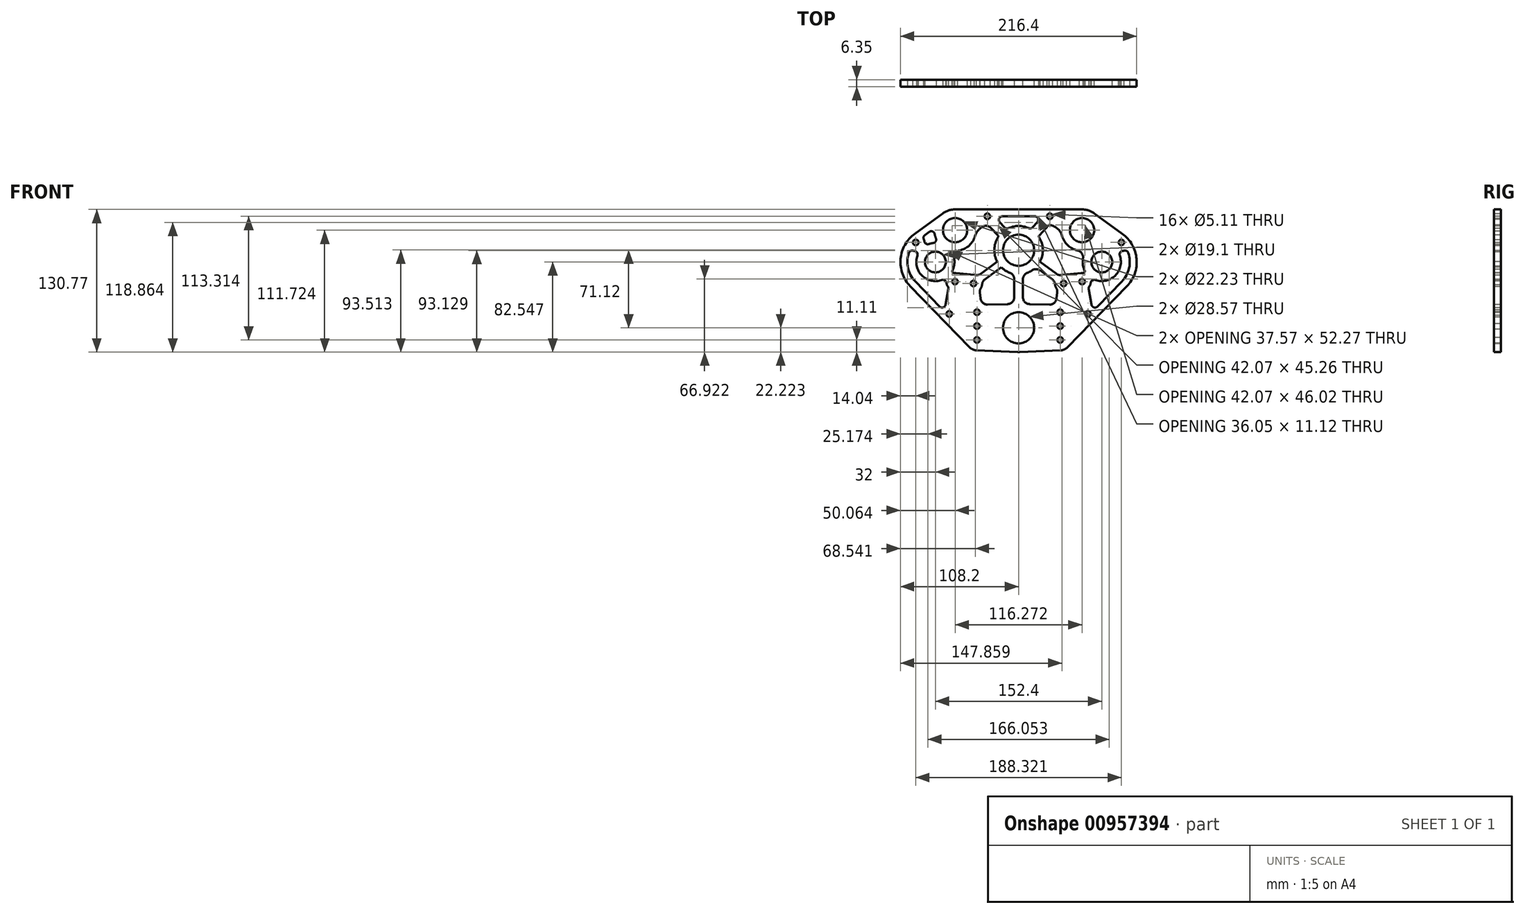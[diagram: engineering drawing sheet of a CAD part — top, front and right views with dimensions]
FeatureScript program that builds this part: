
annotation { "Feature Type Name" : "Feature", "Feature Type Description" : "" }
export const myFeature = defineFeature(function(context is Context, id is Id, definition is map)
    precondition{}
    {
        {
            var Q0;
            Q0=qCreatedBy(makeId("Front.planeOp"),FACE);
            var sketch = newSketch(context, id + "F0", { "sketchPlane" : qUnion([Q0])});
            skCircle(sketch, "E0", {"center": v(-76.2, 58.74) * mm, "radius": 32 * mm, "construction": true});
            skCircle(sketch, "E1", {"center": v(76.2, 58.74) * mm, "radius": 32 * mm, "construction": true});
            skLineSegment(sketch, "E2", {"start": v(-76.2, 58.74) * mm, "end": v(76.2, 58.74) * mm, "construction": true});
            skLineSegment(sketch, "E3", {"start": v(0, 58.74) * mm, "end": v(0, 0) * mm, "construction": true});
            skCircle(sketch, "E4", {"center": v(-76.2, 58.74) * mm, "radius": 7.63 * mm, "construction": true});
            skCircle(sketch, "E5", {"center": v(76.2, 58.74) * mm, "radius": 7.63 * mm, "construction": true});
            skLineSegment(sketch, "E6.bottom", {"start": v(-127, 23.81) * mm, "end": v(127, 23.81) * mm, "construction": true});
            skLineSegment(sketch, "E6.top", {"start": v(-127, -26.99) * mm, "end": v(127, -26.99) * mm, "construction": true});
            skLineSegment(sketch, "E6.left", {"start": v(-127, 23.81) * mm, "end": v(-127, -26.99) * mm, "construction": true});
            skLineSegment(sketch, "E6.right", {"start": v(127, 23.81) * mm, "end": v(127, -26.99) * mm, "construction": true});
            skPoint(sketch, "E6.middle", {"position": v(0, -1.59) * mm});
            skCircle(sketch, "E7", {"center": v(0, 0) * mm, "radius": 50.8 * mm, "construction": true});
            skCircle(sketch, "E8", {"center": v(-58.14, 87.91) * mm, "radius": 26.68 * mm, "construction": true});
            skCircle(sketch, "E9", {"center": v(58.14, 87.91) * mm, "radius": 26.68 * mm, "construction": true});
            skCircle(sketch, "E10", {"center": v(0, 69.53) * mm, "radius": 34.3 * mm, "construction": true});
            skCircle(sketch, "E11", {"center": v(0, 69.53) * mm, "radius": 25.4 * mm, "construction": true});
            skCircle(sketch, "E12", {"center": v(0, 69.53) * mm, "radius": 38.1 * mm, "construction": true});
            skCircle(sketch, "E13", {"center": v(0, -1.59) * mm, "radius": 33.02 * mm, "construction": true});
            skCircle(sketch, "E14", {"center": v(0, -1.59) * mm, "radius": 45.72 * mm, "construction": true});
            skCircle(sketch, "E15", {"center": v(-76.2, 58.74) * mm, "radius": 9.55 * mm});
            skCircle(sketch, "E16", {"center": v(76.2, 58.74) * mm, "radius": 9.55 * mm});
            skCircle(sketch, "E17", {"center": v(-58.14, 87.91) * mm, "radius": 11.11 * mm});
            skCircle(sketch, "E18", {"center": v(58.14, 87.91) * mm, "radius": 11.11 * mm});
            skCircle(sketch, "E19", {"center": v(0, 69.53) * mm, "radius": 14.29 * mm});
            skCircle(sketch, "E20", {"center": v(0, -1.59) * mm, "radius": 14.29 * mm});
            skCircle(sketch, "E21", {"center": v(-38.1, 12.7) * mm, "radius": 9.53 * mm, "construction": true});
            skCircle(sketch, "E22", {"center": v(-38.1, -12.7) * mm, "radius": 9.53 * mm, "construction": true});
            skCircle(sketch, "E23", {"center": v(38.1, -12.7) * mm, "radius": 9.53 * mm, "construction": true});
            skCircle(sketch, "E24", {"center": v(38.1, 12.7) * mm, "radius": 9.53 * mm, "construction": true});
            skCircle(sketch, "E25", {"center": v(38.1, 0) * mm, "radius": 9.53 * mm, "construction": true});
            skCircle(sketch, "E26", {"center": v(-38.1, 0) * mm, "radius": 9.53 * mm, "construction": true});
            skCircle(sketch, "E27", {"center": v(38.1, -12.7) * mm, "radius": 2.55 * mm});
            skCircle(sketch, "E28", {"center": v(38.1, 0) * mm, "radius": 2.55 * mm});
            skCircle(sketch, "E29", {"center": v(38.1, 12.7) * mm, "radius": 2.55 * mm});
            skCircle(sketch, "E30", {"center": v(-38.1, 12.7) * mm, "radius": 2.55 * mm});
            skCircle(sketch, "E31", {"center": v(-38.1, 0) * mm, "radius": 2.55 * mm});
            skCircle(sketch, "E32", {"center": v(-38.1, -12.7) * mm, "radius": 2.55 * mm});
            skLineSegment(sketch, "E33", {"start": v(-44.93, -19.34) * mm, "end": v(-99.15, 36.43) * mm});
            skArc(sketch, "E34", {"start": v(-44.93, -19.34) * mm, "mid": v(-42, -21.4) * mm, "end": v(-38.5, -22.22) * mm});
            skArc(sketch, "E35", {"start": v(38.5, -22.22) * mm, "mid": v(42, -21.4) * mm, "end": v(44.93, -19.34) * mm});
            skLineSegment(sketch, "E36", {"start": v(44.93, -19.34) * mm, "end": v(99.15, 36.43) * mm});
            skCircle(sketch, "E37", {"center": v(58.14, 87.91) * mm, "radius": 19.05 * mm, "construction": true});
            skCircle(sketch, "E38", {"center": v(-58.14, 87.91) * mm, "radius": 19.05 * mm, "construction": true});
            skArc(sketch, "E39", {"start": v(99.15, 36.43) * mm, "mid": v(108.09, 61.46) * mm, "end": v(95.04, 84.61) * mm});
            skArc(sketch, "E40", {"start": v(-95.04, 84.61) * mm, "mid": v(-108.09, 61.46) * mm, "end": v(-99.15, 36.43) * mm});
            skLineSegment(sketch, "E41", {"start": v(-58.24, 40.78) * mm, "end": v(-76.2, 58.74) * mm, "construction": true});
            skLineSegment(sketch, "E42", {"start": v(-76.2, 58.74) * mm, "end": v(-94.16, 76.7) * mm, "construction": true});
            skCircle(sketch, "E43", {"center": v(-94.16, 76.7) * mm, "radius": 2.55 * mm});
            skCircle(sketch, "E44", {"center": v(-58.24, 40.78) * mm, "radius": 2.55 * mm});
            skCircle(sketch, "E45.MirrorC", {"center": v(58.24, 40.78) * mm, "radius": 2.55 * mm});
            skLineSegment(sketch, "E46.MirrorCS", {"start": v(58.24, 40.78) * mm, "end": v(76.2, 58.74) * mm, "construction": true});
            skLineSegment(sketch, "E47.MirrorCS", {"start": v(76.2, 58.74) * mm, "end": v(94.16, 76.7) * mm, "construction": true});
            skCircle(sketch, "E48.MirrorC", {"center": v(94.16, 76.7) * mm, "radius": 2.55 * mm});
            skLineSegment(sketch, "E49", {"start": v(95.04, 84.61) * mm, "end": v(69.35, 103.31) * mm});
            skLineSegment(sketch, "E50", {"start": v(-95.04, 84.61) * mm, "end": v(-69.35, 103.31) * mm});
            skLineSegment(sketch, "E51", {"start": v(-58.14, 106.96) * mm, "end": v(58.14, 106.96) * mm});
            skArc(sketch, "E52", {"start": v(-69.35, 103.31) * mm, "mid": v(-64.03, 106.03) * mm, "end": v(-58.14, 106.96) * mm});
            skArc(sketch, "E53", {"start": v(58.14, 106.96) * mm, "mid": v(64.03, 106.03) * mm, "end": v(69.35, 103.31) * mm});
            skCircle(sketch, "E54", {"center": v(0, -1.59) * mm, "radius": 22.23 * mm, "construction": true});
            skLineSegment(sketch, "E55", {"start": v(38.5, -22.22) * mm, "end": v(0.93, -23.8) * mm});
            skLineSegment(sketch, "E56", {"start": v(-38.5, -22.22) * mm, "end": v(-0.93, -23.8) * mm});
            skArc(sketch, "E57", {"start": v(-0.93, -23.8) * mm, "mid": v(0, -23.81) * mm, "end": v(0.93, -23.8) * mm});
            skLineSegment(sketch, "E58.bottom", {"start": v(-38.1, -12.7) * mm, "end": v(38.1, -12.7) * mm, "construction": true});
            skLineSegment(sketch, "E58.top", {"start": v(-38.1, 12.7) * mm, "end": v(38.1, 12.7) * mm, "construction": true});
            skLineSegment(sketch, "E58.left", {"start": v(-38.1, -12.7) * mm, "end": v(-38.1, 12.7) * mm, "construction": true});
            skLineSegment(sketch, "E58.right", {"start": v(38.1, -12.7) * mm, "end": v(38.1, 12.7) * mm, "construction": true});
            skCircle(sketch, "E59", {"center": v(-28.58, 100.61) * mm, "radius": 6.35 * mm, "construction": true});
            skCircle(sketch, "E60", {"center": v(-28.58, 100.61) * mm, "radius": 2.55 * mm});
            skCircle(sketch, "E61.MirrorC", {"center": v(28.57, 100.61) * mm, "radius": 6.35 * mm, "construction": true});
            skCircle(sketch, "E62.MirrorC", {"center": v(28.57, 100.61) * mm, "radius": 2.55 * mm});
            skCircle(sketch, "E63", {"center": v(-63.5, 11.15) * mm, "radius": 7.94 * mm, "construction": true});
            skCircle(sketch, "E64", {"center": v(-63.5, 11.15) * mm, "radius": 2.55 * mm});
            skCircle(sketch, "E65.MirrorC", {"center": v(63.5, 11.15) * mm, "radius": 7.94 * mm, "construction": true});
            skCircle(sketch, "E66.MirrorC", {"center": v(63.5, 11.15) * mm, "radius": 2.55 * mm});
            skCircle(sketch, "E67", {"center": v(-41.28, 39.05) * mm, "radius": 6.35 * mm, "construction": true});
            skCircle(sketch, "E68", {"center": v(41.28, 39.05) * mm, "radius": 6.35 * mm, "construction": true});
            skCircle(sketch, "E69", {"center": v(41.28, 39.05) * mm, "radius": 2.55 * mm});
            skCircle(sketch, "E70", {"center": v(-41.28, 39.05) * mm, "radius": 2.55 * mm});
            skLineSegment(sketch, "E71", {"start": v(41.28, 39.05) * mm, "end": v(-41.28, 39.05) * mm, "construction": true});
            skLineSegment(sketch, "E72", {"start": v(0, 39.05) * mm, "end": v(0, 69.53) * mm, "construction": true});
            skSolve(sketch);
        }
        {
            var Q0;
            Q0 = qSketchRegion(id + "F0", true);
            extrude(context, id + "F1", {"entities" : qUnion([Q0]), "depth" : 6.35 * mm, "offsetDistance" : 25.4 * mm});
        }
        {
            var Q0;
            Q0=makeQuery(id+"F1.opExtrude","CAP_FACE",FACE,{"disambiguationData":[OSD([sQuery(id+"F0.wireOp",EDGE,"E15"),sQuery(id+"F0.wireOp",EDGE,"E16"),sQuery(id+"F0.wireOp",EDGE,"E17"),sQuery(id+"F0.wireOp",EDGE,"E18"),sQuery(id+"F0.wireOp",EDGE,"E19"),sQuery(id+"F0.wireOp",EDGE,"E20"),sQuery(id+"F0.wireOp",EDGE,"E27"),sQuery(id+"F0.wireOp",EDGE,"E28"),sQuery(id+"F0.wireOp",EDGE,"E29"),sQuery(id+"F0.wireOp",EDGE,"E30"),sQuery(id+"F0.wireOp",EDGE,"E31"),sQuery(id+"F0.wireOp",EDGE,"E32"),sQuery(id+"F0.wireOp",EDGE,"E33"),sQuery(id+"F0.wireOp",EDGE,"E34"),sQuery(id+"F0.wireOp",EDGE,"E35"),sQuery(id+"F0.wireOp",EDGE,"E36"),sQuery(id+"F0.wireOp",EDGE,"E39"),sQuery(id+"F0.wireOp",EDGE,"E40"),sQuery(id+"F0.wireOp",EDGE,"E43"),sQuery(id+"F0.wireOp",EDGE,"E44"),sQuery(id+"F0.wireOp",EDGE,"E45.MirrorC"),sQuery(id+"F0.wireOp",EDGE,"E48.MirrorC"),sQuery(id+"F0.wireOp",EDGE,"E49"),sQuery(id+"F0.wireOp",EDGE,"E50"),sQuery(id+"F0.wireOp",EDGE,"E51"),sQuery(id+"F0.wireOp",EDGE,"E52"),sQuery(id+"F0.wireOp",EDGE,"E53"),sQuery(id+"F0.wireOp",EDGE,"E55"),sQuery(id+"F0.wireOp",EDGE,"E56"),sQuery(id+"F0.wireOp",EDGE,"E57"),sQuery(id+"F0.wireOp",EDGE,"E60"),sQuery(id+"F0.wireOp",EDGE,"E62.MirrorC"),sQuery(id+"F0.wireOp",EDGE,"E64"),sQuery(id+"F0.wireOp",EDGE,"E66.MirrorC"),sQuery(id+"F0.wireOp",EDGE,"E69"),sQuery(id+"F0.wireOp",EDGE,"E70")])],"isStart":false});
            var sketch = newSketch(context, id + "F2", { "sketchPlane" : qUnion([Q0])});
            skCircle(sketch, "E73", {"center": v(-58.14, 87.91) * mm, "radius": 19.05 * mm, "construction": true});
            skCircle(sketch, "E74", {"center": v(0, 69.53) * mm, "radius": 22.23 * mm, "construction": true});
            skCircle(sketch, "E75", {"center": v(58.14, 87.91) * mm, "radius": 19.05 * mm, "construction": true});
            skCircle(sketch, "E76", {"center": v(76.2, 58.74) * mm, "radius": 17.49 * mm, "construction": true});
            skCircle(sketch, "E77", {"center": v(94.16, 76.7) * mm, "radius": 7.94 * mm, "construction": true});
            skCircle(sketch, "E78", {"center": v(58.24, 40.78) * mm, "radius": 7.94 * mm, "construction": true});
            skCircle(sketch, "E79", {"center": v(41.28, 39.05) * mm, "radius": 7.94 * mm, "construction": true});
            skCircle(sketch, "E80", {"center": v(63.5, 11.15) * mm, "radius": 7.94 * mm, "construction": true});
            skCircle(sketch, "E81", {"center": v(38.1, 12.7) * mm, "radius": 7.94 * mm, "construction": true});
            skCircle(sketch, "E82", {"center": v(38.1, 0) * mm, "radius": 7.94 * mm, "construction": true});
            skCircle(sketch, "E83", {"center": v(38.1, -12.7) * mm, "radius": 7.94 * mm, "construction": true});
            skCircle(sketch, "E84", {"center": v(-38.1, 12.7) * mm, "radius": 7.94 * mm, "construction": true});
            skCircle(sketch, "E85", {"center": v(-38.1, 0) * mm, "radius": 7.94 * mm, "construction": true});
            skCircle(sketch, "E86", {"center": v(-38.1, -12.7) * mm, "radius": 7.94 * mm, "construction": true});
            skCircle(sketch, "E87", {"center": v(-63.5, 11.15) * mm, "radius": 7.94 * mm, "construction": true});
            skCircle(sketch, "E88", {"center": v(-41.28, 39.05) * mm, "radius": 7.94 * mm, "construction": true});
            skCircle(sketch, "E89", {"center": v(-58.24, 40.78) * mm, "radius": 7.94 * mm, "construction": true});
            skCircle(sketch, "E90", {"center": v(-76.2, 58.74) * mm, "radius": 17.49 * mm, "construction": true});
            skCircle(sketch, "E91", {"center": v(-94.16, 76.7) * mm, "radius": 7.94 * mm, "construction": true});
            skCircle(sketch, "E92", {"center": v(-28.58, 100.61) * mm, "radius": 7.94 * mm, "construction": true});
            skCircle(sketch, "E93", {"center": v(28.57, 100.61) * mm, "radius": 7.94 * mm, "construction": true});
            skCircle(sketch, "E94", {"center": v(0, -1.59) * mm, "radius": 22.23 * mm, "construction": true});
            skLineSegment(sketch, "E95", {"start": v(-99.15, 36.43) * mm, "end": v(-44.93, -19.34) * mm, "construction": true});
            skLineSegment(sketch, "E96", {"start": v(-38.5, -22.22) * mm, "end": v(-0.93, -23.8) * mm, "construction": true});
            skLineSegment(sketch, "E97", {"start": v(0.93, -23.8) * mm, "end": v(38.5, -22.22) * mm, "construction": true});
            skLineSegment(sketch, "E98", {"start": v(44.93, -19.34) * mm, "end": v(99.15, 36.43) * mm, "construction": true});
            skLineSegment(sketch, "E99", {"start": v(95.04, 84.61) * mm, "end": v(69.35, 103.31) * mm, "construction": true});
            skLineSegment(sketch, "E100", {"start": v(58.14, 106.96) * mm, "end": v(-58.14, 106.96) * mm, "construction": true});
            skLineSegment(sketch, "E101", {"start": v(-69.35, 103.31) * mm, "end": v(-95.04, 84.61) * mm, "construction": true});
            skArc(sketch, "E102", {"start": v(-58.14, 106.96) * mm, "mid": v(-64.03, 106.03) * mm, "end": v(-69.35, 103.31) * mm, "construction": true});
            skArc(sketch, "E103", {"start": v(-95.04, 84.61) * mm, "mid": v(-108.09, 61.46) * mm, "end": v(-99.15, 36.43) * mm, "construction": true});
            skArc(sketch, "E104", {"start": v(-44.93, -19.34) * mm, "mid": v(-42, -21.4) * mm, "end": v(-38.5, -22.22) * mm, "construction": true});
            skArc(sketch, "E105", {"start": v(-0.93, -23.8) * mm, "mid": v(0, -23.81) * mm, "end": v(0.93, -23.8) * mm, "construction": true});
            skArc(sketch, "E106", {"start": v(38.5, -22.22) * mm, "mid": v(42, -21.4) * mm, "end": v(44.93, -19.34) * mm, "construction": true});
            skArc(sketch, "E107", {"start": v(99.15, 36.43) * mm, "mid": v(108.09, 61.46) * mm, "end": v(95.04, 84.61) * mm, "construction": true});
            skLineSegment(sketch, "E108.0", {"start": v(58.14, 100.61) * mm, "end": v(-58.14, 100.61) * mm, "construction": true});
            skArc(sketch, "E108.1", {"start": v(58.14, 100.61) * mm, "mid": v(62.07, 99.99) * mm, "end": v(65.61, 98.18) * mm, "construction": true});
            skLineSegment(sketch, "E108.2", {"start": v(91.3, 79.48) * mm, "end": v(65.61, 98.18) * mm, "construction": true});
            skArc(sketch, "E108.3", {"start": v(-40.38, -14.91) * mm, "mid": v(-39.4, -15.6) * mm, "end": v(-38.23, -15.87) * mm, "construction": true});
            skLineSegment(sketch, "E108.4", {"start": v(-94.6, 40.85) * mm, "end": v(-40.38, -14.91) * mm, "construction": true});
            skArc(sketch, "E108.5", {"start": v(-91.3, 79.48) * mm, "mid": v(-101.76, 60.92) * mm, "end": v(-94.6, 40.85) * mm, "construction": true});
            skLineSegment(sketch, "E108.6", {"start": v(-65.61, 98.18) * mm, "end": v(-91.3, 79.48) * mm, "construction": true});
            skLineSegment(sketch, "E108.7", {"start": v(-38.23, -15.87) * mm, "end": v(-0.67, -17.45) * mm, "construction": true});
            skArc(sketch, "E108.8", {"start": v(-0.67, -17.45) * mm, "mid": v(0, -17.46) * mm, "end": v(0.67, -17.45) * mm, "construction": true});
            skLineSegment(sketch, "E108.9", {"start": v(0.67, -17.45) * mm, "end": v(38.23, -15.87) * mm, "construction": true});
            skArc(sketch, "E108.10", {"start": v(-58.14, 100.61) * mm, "mid": v(-62.07, 99.99) * mm, "end": v(-65.61, 98.18) * mm, "construction": true});
            skArc(sketch, "E108.11", {"start": v(38.23, -15.87) * mm, "mid": v(39.4, -15.6) * mm, "end": v(40.38, -14.91) * mm, "construction": true});
            skLineSegment(sketch, "E108.12", {"start": v(40.38, -14.91) * mm, "end": v(94.6, 40.85) * mm, "construction": true});
            skArc(sketch, "E108.13", {"start": v(94.6, 40.85) * mm, "mid": v(101.76, 60.92) * mm, "end": v(91.3, 79.48) * mm, "construction": true});
            skArc(sketch, "E109", {"start": v(-59, 61.93) * mm, "mid": v(-58.88, 56.32) * mm, "end": v(-60.53, 50.97) * mm});
            skArc(sketch, "E110", {"start": v(-58.97, 48.68) * mm, "mid": v(-58.2, 48.71) * mm, "end": v(-57.44, 48.67) * mm});
            skLineSegment(sketch, "E111", {"start": v(-57.44, 48.67) * mm, "end": v(-40.47, 46.95) * mm});
            skLineSegment(sketch, "E112", {"start": v(-41.28, 39.05) * mm, "end": v(0, 69.53) * mm, "construction": true});
            skLineSegment(sketch, "E113", {"start": v(-34.6, 47.93) * mm, "end": v(-19.58, 59.02) * mm});
            skLineSegment(sketch, "E114", {"start": v(-33.54, 40.82) * mm, "end": v(-15.8, 53.91) * mm});
            skLineSegment(sketch, "E115", {"start": v(-28.45, 52.47) * mm, "end": v(-26.56, 49.92) * mm, "construction": true});
            skLineSegment(sketch, "E116", {"start": v(-24.67, 47.37) * mm, "end": v(-26.56, 49.92) * mm, "construction": true});
            skArc(sketch, "E117", {"start": v(-40.47, 46.95) * mm, "mid": v(-40.06, 46.9) * mm, "end": v(-39.66, 46.82) * mm});
            skArc(sketch, "E118", {"start": v(-19.58, 59.02) * mm, "mid": v(-22.21, 70.25) * mm, "end": v(-18.86, 81.3) * mm});
            skLineSegment(sketch, "E119", {"start": v(0, 69.53) * mm, "end": v(-28.58, 100.61) * mm, "construction": true});
            skLineSegment(sketch, "E120", {"start": v(-19.04, 83.2) * mm, "end": v(-25.2, 89.9) * mm});
            skArc(sketch, "E121", {"start": v(-32.76, 91.25) * mm, "mid": v(-37.18, 87.69) * mm, "end": v(-39.82, 82.66) * mm});
            skArc(sketch, "E122", {"start": v(-54.1, 69.3) * mm, "mid": v(-45.12, 74) * mm, "end": v(-39.82, 82.66) * mm});
            skPoint(sketch, "E123.visualSharp", {"position": v(-62.28, 69.32) * mm});
            skArc(sketch, "E123.filletArc", {"start": v(-54.1, 69.3) * mm, "mid": v(-58.05, 66.6) * mm, "end": v(-59, 61.93) * mm});
            skPoint(sketch, "E124.visualSharp", {"position": v(-37.3, 45.93) * mm});
            skArc(sketch, "E124.filletArc", {"start": v(-39.66, 46.82) * mm, "mid": v(-37, 46.84) * mm, "end": v(-34.6, 47.93) * mm});
            skPoint(sketch, "E125.visualSharp", {"position": v(-63.47, 46.75) * mm});
            skArc(sketch, "E125.filletArc", {"start": v(-60.53, 50.97) * mm, "mid": v(-60.42, 49.36) * mm, "end": v(-58.97, 48.68) * mm});
            skPoint(sketch, "E126.visualSharp", {"position": v(-18.2, 82.3) * mm});
            skArc(sketch, "E126.filletArc", {"start": v(-18.86, 81.3) * mm, "mid": v(-18.63, 82.28) * mm, "end": v(-19.04, 83.2) * mm});
            skLineSegment(sketch, "E127", {"start": v(0, 69.53) * mm, "end": v(0, 0) * mm, "construction": true});
            skArc(sketch, "E128.MirrorCS", {"start": v(58.97, 48.68) * mm, "mid": v(58.2, 48.71) * mm, "end": v(57.44, 48.67) * mm});
            skArc(sketch, "E129.MirrorCS", {"start": v(60.53, 50.97) * mm, "mid": v(60.42, 49.36) * mm, "end": v(58.97, 48.68) * mm});
            skArc(sketch, "E130.MirrorCS", {"start": v(18.86, 81.3) * mm, "mid": v(18.63, 82.28) * mm, "end": v(19.04, 83.2) * mm});
            skLineSegment(sketch, "E131.MirrorCS", {"start": v(28.45, 52.47) * mm, "end": v(26.56, 49.92) * mm, "construction": true});
            skArc(sketch, "E132.MirrorCS", {"start": v(40.47, 46.95) * mm, "mid": v(40.06, 46.9) * mm, "end": v(39.66, 46.82) * mm});
            skArc(sketch, "E133.MirrorCS", {"start": v(39.66, 46.82) * mm, "mid": v(37, 46.84) * mm, "end": v(34.6, 47.93) * mm});
            skLineSegment(sketch, "E134.MirrorCS", {"start": v(24.67, 47.37) * mm, "end": v(26.56, 49.92) * mm, "construction": true});
            skArc(sketch, "E135.MirrorCS", {"start": v(54.1, 69.3) * mm, "mid": v(45.12, 74) * mm, "end": v(39.82, 82.66) * mm});
            skArc(sketch, "E136.MirrorCS", {"start": v(19.58, 59.02) * mm, "mid": v(22.21, 70.25) * mm, "end": v(18.86, 81.3) * mm});
            skPoint(sketch, "E137.MirrorP", {"position": v(37.3, 45.93) * mm});
            skLineSegment(sketch, "E138.MirrorCS", {"start": v(57.44, 48.67) * mm, "end": v(40.47, 46.95) * mm});
            skArc(sketch, "E139.MirrorCS", {"start": v(27.78, 92.72) * mm, "mid": v(35.35, 89.54) * mm, "end": v(39.82, 82.66) * mm});
            skLineSegment(sketch, "E140.MirrorCS", {"start": v(33.54, 40.82) * mm, "end": v(15.8, 53.91) * mm});
            skPoint(sketch, "E141.MirrorP", {"position": v(63.47, 46.75) * mm});
            skLineSegment(sketch, "E142.MirrorCS", {"start": v(34.6, 47.93) * mm, "end": v(19.58, 59.02) * mm});
            skArc(sketch, "E143.MirrorCS", {"start": v(54.1, 69.3) * mm, "mid": v(58.05, 66.6) * mm, "end": v(59, 61.93) * mm});
            skLineSegment(sketch, "E144.MirrorCS", {"start": v(19.04, 83.2) * mm, "end": v(27.78, 92.72) * mm});
            skPoint(sketch, "E145.MirrorP", {"position": v(18.2, 82.3) * mm});
            skArc(sketch, "E146.MirrorCS", {"start": v(59, 61.93) * mm, "mid": v(58.88, 56.32) * mm, "end": v(60.53, 50.97) * mm});
            skLineSegment(sketch, "E147.MirrorCS", {"start": v(-58.14, 100.61) * mm, "end": v(58.14, 100.61) * mm, "construction": true});
            skPoint(sketch, "E148.MirrorP", {"position": v(62.28, 69.32) * mm});
            skLineSegment(sketch, "E149", {"start": v(-11.19, 88.74) * mm, "end": v(-20.77, 99.16) * mm, "construction": true});
            skLineSegment(sketch, "E150", {"start": v(11.19, 88.74) * mm, "end": v(20.77, 99.16) * mm, "construction": true});
            skArc(sketch, "E151", {"start": v(-9.18, 89.77) * mm, "mid": v(0, 91.76) * mm, "end": v(9.18, 89.77) * mm});
            skLineSegment(sketch, "E152", {"start": v(0, 69.53) * mm, "end": v(28.57, 100.61) * mm, "construction": true});
            skLineSegment(sketch, "E153", {"start": v(0, 69.53) * mm, "end": v(41.28, 39.05) * mm, "construction": true});
            skLineSegment(sketch, "E154", {"start": v(-14.87, 100.61) * mm, "end": v(14.87, 100.61) * mm});
            skLineSegment(sketch, "E155", {"start": v(12.82, 90.52) * mm, "end": v(17.21, 95.29) * mm});
            skLineSegment(sketch, "E156", {"start": v(-12.82, 90.52) * mm, "end": v(-17.21, 95.29) * mm});
            skPoint(sketch, "E157.visualSharp", {"position": v(-22.1, 100.61) * mm});
            skArc(sketch, "E157.filletArc", {"start": v(-14.87, 100.61) * mm, "mid": v(-17.78, 98.71) * mm, "end": v(-17.21, 95.29) * mm});
            skPoint(sketch, "E158.visualSharp", {"position": v(-11.19, 88.74) * mm});
            skArc(sketch, "E158.filletArc", {"start": v(-12.82, 90.52) * mm, "mid": v(-11.12, 89.56) * mm, "end": v(-9.18, 89.77) * mm});
            skPoint(sketch, "E159.visualSharp", {"position": v(11.19, 88.74) * mm});
            skArc(sketch, "E159.filletArc", {"start": v(9.18, 89.77) * mm, "mid": v(11.12, 89.56) * mm, "end": v(12.82, 90.52) * mm});
            skPoint(sketch, "E160.visualSharp", {"position": v(22.1, 100.61) * mm});
            skArc(sketch, "E160.filletArc", {"start": v(17.21, 95.29) * mm, "mid": v(17.78, 98.71) * mm, "end": v(14.87, 100.61) * mm});
            skArc(sketch, "E161", {"start": v(-96.5, 69.12) * mm, "mid": v(-95.87, 68.95) * mm, "end": v(-95.23, 68.83) * mm});
            skArc(sketch, "E162", {"start": v(-92.67, 64.62) * mm, "mid": v(-88.57, 46.37) * mm, "end": v(-70.32, 42.27) * mm});
            skLineSegment(sketch, "E163", {"start": v(-58.24, 40.78) * mm, "end": v(-63.5, 11.15) * mm, "construction": true});
            skLineSegment(sketch, "E164", {"start": v(-64.29, 33.95) * mm, "end": v(-66.83, 19.64) * mm});
            skArc(sketch, "E165", {"start": v(-64.8, 36.3) * mm, "mid": v(-65.65, 37.93) * mm, "end": v(-66.1, 39.7) * mm});
            skArc(sketch, "E166", {"start": v(-68.16, 17.57) * mm, "mid": v(-68.14, 17.6) * mm, "end": v(-68.11, 17.6) * mm});
            skLineSegment(sketch, "E167", {"start": v(-72.3, 17.93) * mm, "end": v(-94.6, 40.85) * mm});
            skArc(sketch, "E168", {"start": v(-100.45, 67.12) * mm, "mid": v(-101.24, 53.16) * mm, "end": v(-94.6, 40.85) * mm});
            skPoint(sketch, "E169.visualSharp", {"position": v(-99.03, 70.43) * mm});
            skArc(sketch, "E169.filletArc", {"start": v(-96.5, 69.12) * mm, "mid": v(-98.88, 68.91) * mm, "end": v(-100.45, 67.12) * mm});
            skPoint(sketch, "E170.visualSharp", {"position": v(-88.93, 70.73) * mm});
            skArc(sketch, "E170.filletArc", {"start": v(-92.67, 64.62) * mm, "mid": v(-92.95, 67.34) * mm, "end": v(-95.23, 68.83) * mm});
            skPoint(sketch, "E171.visualSharp", {"position": v(-64.21, 46) * mm});
            skArc(sketch, "E171.filletArc", {"start": v(-66.1, 39.7) * mm, "mid": v(-67.6, 42) * mm, "end": v(-70.32, 42.27) * mm});
            skPoint(sketch, "E172.visualSharp", {"position": v(-64.04, 35.36) * mm});
            skArc(sketch, "E172.filletArc", {"start": v(-64.29, 33.95) * mm, "mid": v(-64.31, 35.17) * mm, "end": v(-64.8, 36.3) * mm});
            skPoint(sketch, "E173.visualSharp", {"position": v(-67.08, 18.23) * mm});
            skArc(sketch, "E173.filletArc", {"start": v(-68.11, 17.6) * mm, "mid": v(-67.27, 18.5) * mm, "end": v(-66.83, 19.64) * mm});
            skPoint(sketch, "E174.visualSharp", {"position": v(-70.06, 15.62) * mm});
            skArc(sketch, "E174.filletArc", {"start": v(-72.3, 17.93) * mm, "mid": v(-70.3, 16.98) * mm, "end": v(-68.16, 17.57) * mm});
            skArc(sketch, "E175.MirrorCS", {"start": v(68.16, 17.57) * mm, "mid": v(68.14, 17.6) * mm, "end": v(68.11, 17.6) * mm});
            skArc(sketch, "E176.MirrorCS", {"start": v(68.11, 17.6) * mm, "mid": v(67.27, 18.5) * mm, "end": v(66.83, 19.64) * mm});
            skArc(sketch, "E177.MirrorCS", {"start": v(96.5, 69.12) * mm, "mid": v(95.87, 68.95) * mm, "end": v(95.23, 68.83) * mm});
            skArc(sketch, "E178.MirrorCS", {"start": v(64.29, 33.95) * mm, "mid": v(64.31, 35.17) * mm, "end": v(64.8, 36.3) * mm});
            skArc(sketch, "E179.MirrorCS", {"start": v(64.8, 36.3) * mm, "mid": v(65.65, 37.93) * mm, "end": v(66.1, 39.7) * mm});
            skArc(sketch, "E180.MirrorCS", {"start": v(72.3, 17.93) * mm, "mid": v(70.3, 16.98) * mm, "end": v(68.16, 17.57) * mm});
            skArc(sketch, "E181.MirrorCS", {"start": v(92.67, 64.62) * mm, "mid": v(92.95, 67.34) * mm, "end": v(95.23, 68.83) * mm});
            skArc(sketch, "E182.MirrorCS", {"start": v(96.5, 69.12) * mm, "mid": v(98.88, 68.91) * mm, "end": v(100.45, 67.12) * mm});
            skPoint(sketch, "E183.MirrorP", {"position": v(64.21, 46) * mm});
            skLineSegment(sketch, "E184.MirrorCS", {"start": v(72.3, 17.93) * mm, "end": v(94.6, 40.85) * mm});
            skPoint(sketch, "E185.MirrorP", {"position": v(70.06, 15.62) * mm});
            skPoint(sketch, "E186.MirrorP", {"position": v(99.03, 70.43) * mm});
            skArc(sketch, "E187.MirrorCS", {"start": v(100.45, 67.12) * mm, "mid": v(101.24, 53.16) * mm, "end": v(94.6, 40.85) * mm});
            skLineSegment(sketch, "E188.MirrorCS", {"start": v(64.29, 33.95) * mm, "end": v(66.83, 19.64) * mm});
            skPoint(sketch, "E189.MirrorP", {"position": v(88.93, 70.73) * mm});
            skPoint(sketch, "E190.MirrorP", {"position": v(64.04, 35.36) * mm});
            skPoint(sketch, "E191.MirrorP", {"position": v(67.08, 18.23) * mm});
            skArc(sketch, "E192.MirrorCS", {"start": v(92.67, 64.62) * mm, "mid": v(88.57, 46.37) * mm, "end": v(70.32, 42.27) * mm});
            skArc(sketch, "E193.MirrorCS", {"start": v(66.1, 39.7) * mm, "mid": v(67.6, 42) * mm, "end": v(70.32, 42.27) * mm});
            skPoint(sketch, "E194.visualSharp", {"position": v(-27.78, 92.72) * mm});
            skArc(sketch, "E194.filletArc", {"start": v(-25.2, 89.9) * mm, "mid": v(-28.75, 91.85) * mm, "end": v(-32.76, 91.25) * mm});
            skLineSegment(sketch, "E195", {"start": v(-85.76, 83.51) * mm, "end": v(-81.84, 86.36) * mm});
            skArc(sketch, "E196", {"start": v(-76.86, 84.38) * mm, "mid": v(-76.37, 82.4) * mm, "end": v(-75.68, 80.5) * mm});
            skArc(sketch, "E197", {"start": v(-78.24, 76.1) * mm, "mid": v(-80.18, 75.77) * mm, "end": v(-82.08, 75.2) * mm});
            skArc(sketch, "E198", {"start": v(-86.83, 79.73) * mm, "mid": v(-86.5, 78.77) * mm, "end": v(-86.3, 77.77) * mm});
            skPoint(sketch, "E199.visualSharp", {"position": v(-88.1, 81.81) * mm});
            skArc(sketch, "E199.filletArc", {"start": v(-85.76, 83.51) * mm, "mid": v(-86.95, 81.8) * mm, "end": v(-86.83, 79.73) * mm});
            skPoint(sketch, "E200.visualSharp", {"position": v(-72.93, 75.92) * mm});
            skArc(sketch, "E200.filletArc", {"start": v(-78.24, 76.1) * mm, "mid": v(-75.86, 77.66) * mm, "end": v(-75.68, 80.5) * mm});
            skPoint(sketch, "E201.visualSharp", {"position": v(-88.19, 71.47) * mm});
            skArc(sketch, "E201.filletArc", {"start": v(-86.3, 77.77) * mm, "mid": v(-84.8, 75.48) * mm, "end": v(-82.08, 75.2) * mm});
            skPoint(sketch, "E202.visualSharp", {"position": v(-77.1, 89.82) * mm});
            skArc(sketch, "E202.filletArc", {"start": v(-76.86, 84.38) * mm, "mid": v(-78.8, 86.75) * mm, "end": v(-81.84, 86.36) * mm});
            skLineSegment(sketch, "E203", {"start": v(-38.1, 12.7) * mm, "end": v(-63.5, 11.15) * mm, "construction": true});
            skLineSegment(sketch, "E204", {"start": v(-38.58, 20.62) * mm, "end": v(-63.98, 19.07) * mm, "construction": true});
            skArc(sketch, "E205", {"start": v(-63.98, 19.07) * mm, "mid": v(-63.96, 3.22) * mm, "end": v(-62.11, 18.96) * mm, "construction": true});
            skLineSegment(sketch, "E206", {"start": v(63.5, 11.15) * mm, "end": v(58.24, 40.78) * mm, "construction": true});
            skLineSegment(sketch, "E207", {"start": v(38.1, 12.7) * mm, "end": v(63.5, 11.15) * mm, "construction": true});
            skLineSegment(sketch, "E208", {"start": v(58.24, 40.78) * mm, "end": v(41.28, 39.05) * mm, "construction": true});
            skCircle(sketch, "E209.MirrorC", {"center": v(-41.27, 39.05) * mm, "radius": 7.94 * mm, "construction": true});
            skLineSegment(sketch, "E210", {"start": v(-3.97, 47.66) * mm, "end": v(-3.97, 20.28) * mm});
            skLineSegment(sketch, "E211", {"start": v(3.97, 20.28) * mm, "end": v(3.97, 47.66) * mm});
            skLineSegment(sketch, "E212", {"start": v(-3.97, 33.97) * mm, "end": v(0, 33.97) * mm, "construction": true});
            skLineSegment(sketch, "E213", {"start": v(0, 33.97) * mm, "end": v(3.97, 33.97) * mm, "construction": true});
            skArc(sketch, "E214", {"start": v(-3.97, 47.66) * mm, "mid": v(-10.37, 49.88) * mm, "end": v(-15.8, 53.91) * mm});
            skArc(sketch, "E215", {"start": v(3.97, 47.66) * mm, "mid": v(10.37, 49.88) * mm, "end": v(15.8, 53.91) * mm});
            skLineSegment(sketch, "E216", {"start": v(-41.28, 39.05) * mm, "end": v(-38.1, 12.7) * mm, "construction": true});
            skLineSegment(sketch, "E217", {"start": v(-35.79, 33.32) * mm, "end": v(-34.13, 19.57) * mm});
            skLineSegment(sketch, "E218", {"start": v(-34.13, 19.57) * mm, "end": v(-3.97, 20.28) * mm});
            skArc(sketch, "E219", {"start": v(-35.79, 33.32) * mm, "mid": v(-33.67, 36.77) * mm, "end": v(-33.54, 40.82) * mm});
            skArc(sketch, "E220", {"start": v(33.54, 40.82) * mm, "mid": v(33.67, 36.77) * mm, "end": v(35.79, 33.32) * mm});
            skLineSegment(sketch, "E221", {"start": v(35.79, 33.32) * mm, "end": v(34.13, 19.57) * mm});
            skLineSegment(sketch, "E222", {"start": v(3.97, 20.28) * mm, "end": v(34.13, 19.57) * mm});
            skArc(sketch, "E223", {"start": v(-15.8, 53.91) * mm, "mid": v(-10.37, 49.88) * mm, "end": v(-3.97, 47.66) * mm});
            skSolve(sketch);
        }
        {
            var Q0;
            Q0 = qSketchRegion(id + "F2", true);
            extrude(context, id + "F3", {"entities" : qUnion([Q0]), "operationType" : NewBodyOperationType.REMOVE, "endBound" : BoundingType.THROUGH_ALL, "oppositeDirection" : true, "depth" : 25.4 * mm, "offsetDistance" : 25.4 * mm});
        }
        {
            var Q0;
            Q0=makeQuery(id+"F3.boolean.opBoolean","COPY",EDGE,{"derivedFrom":makeQuery(id+"F3.opExtrude","SWEPT_EDGE",EDGE,{"disambiguationData":[OSD([sQuery(id+"F2.wireOp",EDGE,"E114"),sQuery(id+"F2.wireOp",EDGE,"E223")])]})});
            var Q1;
            Q1=makeQuery(id+"F3.boolean.opBoolean","COPY",EDGE,{"derivedFrom":makeQuery(id+"F3.opExtrude","SWEPT_EDGE",EDGE,{"disambiguationData":[OSD([sQuery(id+"F2.wireOp",EDGE,"E114"),sQuery(id+"F2.wireOp",EDGE,"E219")])]})});
            var Q2;
            Q2=makeQuery(id+"F3.boolean.opBoolean","COPY",EDGE,{"derivedFrom":makeQuery(id+"F3.opExtrude","SWEPT_EDGE",EDGE,{"disambiguationData":[OSD([sQuery(id+"F2.wireOp",EDGE,"E217"),sQuery(id+"F2.wireOp",EDGE,"E219")])]})});
            var Q3;
            Q3=makeQuery(id+"F3.boolean.opBoolean","COPY",EDGE,{"derivedFrom":makeQuery(id+"F3.opExtrude","SWEPT_EDGE",EDGE,{"disambiguationData":[OSD([sQuery(id+"F2.wireOp",EDGE,"E210"),sQuery(id+"F2.wireOp",EDGE,"E223")])]})});
            var Q4;
            Q4=makeQuery(id+"F3.boolean.opBoolean","COPY",EDGE,{"derivedFrom":makeQuery(id+"F3.opExtrude","SWEPT_EDGE",EDGE,{"disambiguationData":[OSD([sQuery(id+"F2.wireOp",EDGE,"E210"),sQuery(id+"F2.wireOp",EDGE,"E218")])]})});
            var Q5;
            Q5=makeQuery(id+"F3.boolean.opBoolean","COPY",EDGE,{"derivedFrom":makeQuery(id+"F3.opExtrude","SWEPT_EDGE",EDGE,{"disambiguationData":[OSD([sQuery(id+"F2.wireOp",EDGE,"E217"),sQuery(id+"F2.wireOp",EDGE,"E218")])]})});
            var Q6;
            Q6=makeQuery(id+"F3.boolean.opBoolean","COPY",EDGE,{"derivedFrom":makeQuery(id+"F3.opExtrude","SWEPT_EDGE",EDGE,{"disambiguationData":[OSD([sQuery(id+"F2.wireOp",EDGE,"E211"),sQuery(id+"F2.wireOp",EDGE,"E222")])]})});
            var Q7;
            Q7=makeQuery(id+"F3.boolean.opBoolean","COPY",EDGE,{"derivedFrom":makeQuery(id+"F3.opExtrude","SWEPT_EDGE",EDGE,{"disambiguationData":[OSD([sQuery(id+"F2.wireOp",EDGE,"E211"),sQuery(id+"F2.wireOp",EDGE,"E215")])]})});
            var Q8;
            Q8=makeQuery(id+"F3.boolean.opBoolean","COPY",EDGE,{"derivedFrom":makeQuery(id+"F3.opExtrude","SWEPT_EDGE",EDGE,{"disambiguationData":[OSD([sQuery(id+"F2.wireOp",EDGE,"E140.MirrorCS"),sQuery(id+"F2.wireOp",EDGE,"E215")])]})});
            var Q9;
            Q9=makeQuery(id+"F3.boolean.opBoolean","COPY",EDGE,{"derivedFrom":makeQuery(id+"F3.opExtrude","SWEPT_EDGE",EDGE,{"disambiguationData":[OSD([sQuery(id+"F2.wireOp",EDGE,"E140.MirrorCS"),sQuery(id+"F2.wireOp",EDGE,"E220")])]})});
            var Q10;
            Q10=makeQuery(id+"F3.boolean.opBoolean","COPY",EDGE,{"derivedFrom":makeQuery(id+"F3.opExtrude","SWEPT_EDGE",EDGE,{"disambiguationData":[OSD([sQuery(id+"F2.wireOp",EDGE,"E220"),sQuery(id+"F2.wireOp",EDGE,"E221")])]})});
            var Q11;
            Q11=makeQuery(id+"F3.boolean.opBoolean","COPY",EDGE,{"derivedFrom":makeQuery(id+"F3.opExtrude","SWEPT_EDGE",EDGE,{"disambiguationData":[OSD([sQuery(id+"F2.wireOp",EDGE,"E221"),sQuery(id+"F2.wireOp",EDGE,"E222")])]})});
            fillet(context, id + "F4", {"entities" : qUnion([Q0, Q1, Q2, Q3, Q4, Q5, Q6, Q7, Q8, Q9, Q10, Q11]), "radius" : 6.35 * mm, "tangentPropagation" : true, "allowEdgeOverflow" : false});
        }
    });
